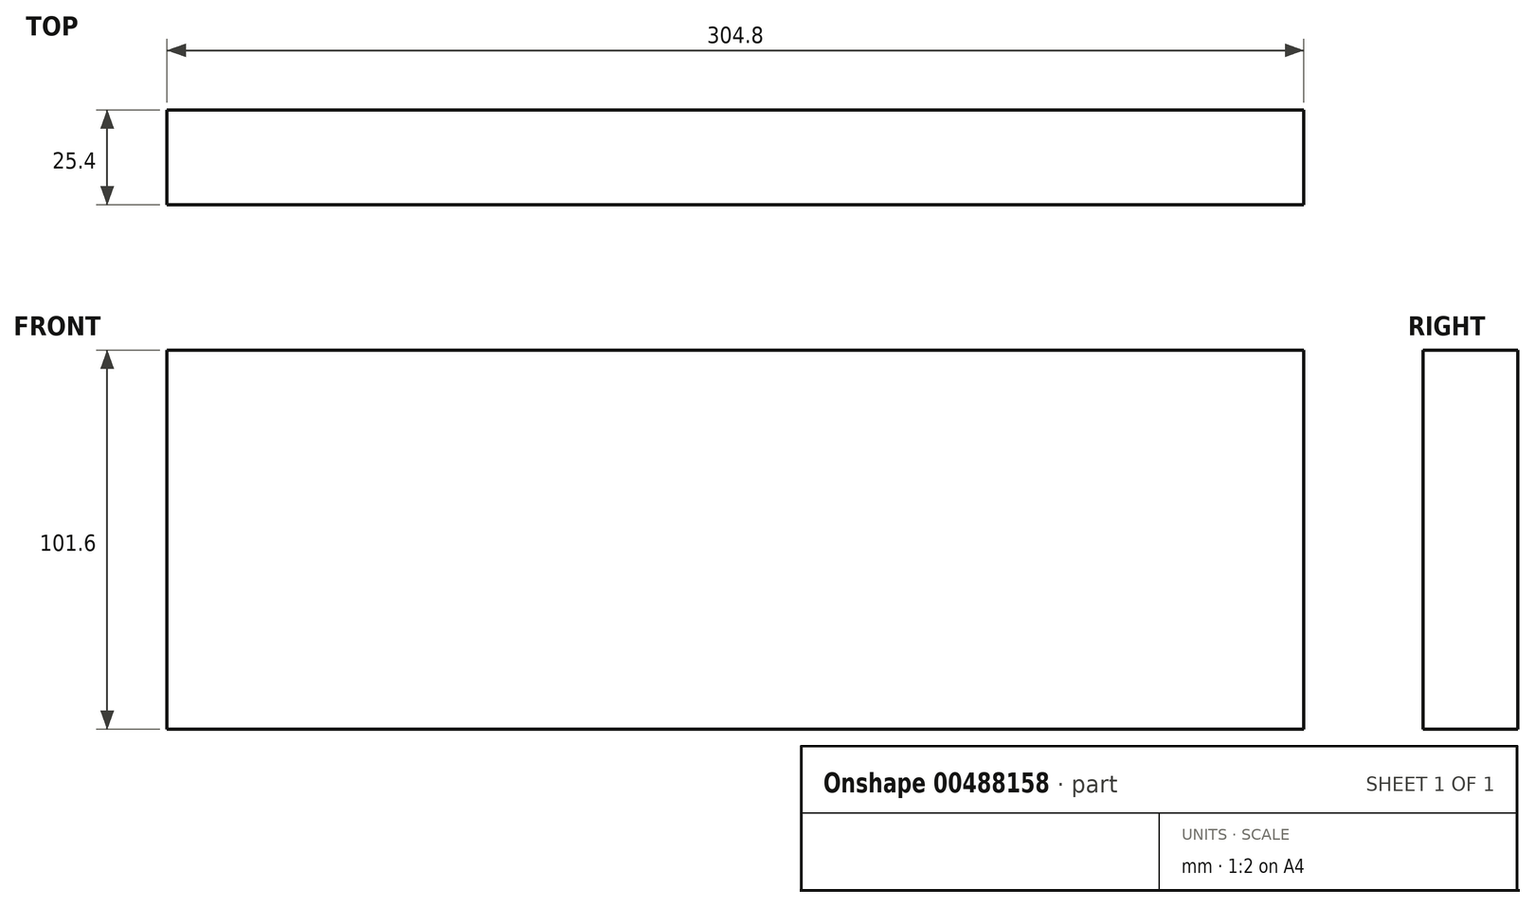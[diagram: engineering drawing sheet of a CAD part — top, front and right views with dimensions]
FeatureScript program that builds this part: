
annotation { "Feature Type Name" : "Feature", "Feature Type Description" : "" }
export const myFeature = defineFeature(function(context is Context, id is Id, definition is map)
    precondition{}
    {
        {
            var Q0;
            Q0=qCreatedBy(makeId("Front.planeOp"),FACE);
            var sketch = newSketch(context, id + "F0", { "sketchPlane" : qUnion([Q0])});
            skLineSegment(sketch, "E0.bottom", {"start": v(0, 0) * mm, "end": v(304.8, 0) * mm});
            skLineSegment(sketch, "E0.top", {"start": v(0, 101.6) * mm, "end": v(304.8, 101.6) * mm});
            skLineSegment(sketch, "E0.left", {"start": v(0, 0) * mm, "end": v(0, 101.6) * mm});
            skLineSegment(sketch, "E0.right", {"start": v(304.8, 0) * mm, "end": v(304.8, 101.6) * mm});
            skSolve(sketch);
        }
        {
            var Q0;
            Q0=makeQuery(id+"F0.imprint","IMPRINT",FACE,{"disambiguationData":[TD([[makeQuery(id+"F0.imprint","IMPRINT",EDGE,{"derivedFrom":sQuery(id+"F0.wireOp",EDGE,"E0.bottom")}),1.0]])]});
            extrude(context, id + "F1", {"entities" : qUnion([Q0]), "depth" : 25.4 * mm, "offsetDistance" : 25.4 * mm});
        }
    });
